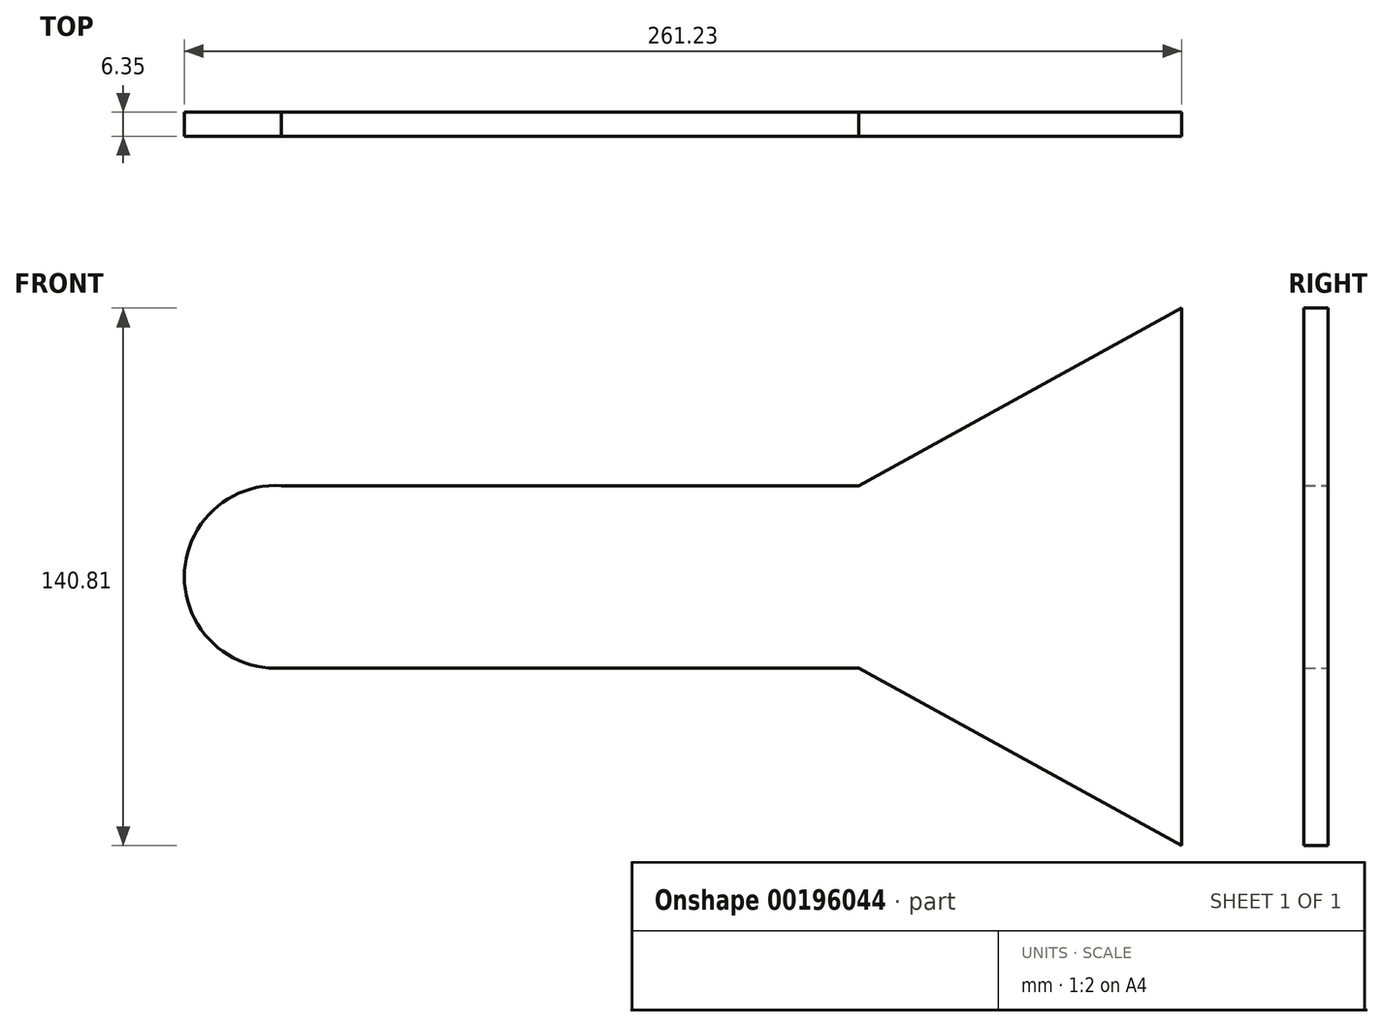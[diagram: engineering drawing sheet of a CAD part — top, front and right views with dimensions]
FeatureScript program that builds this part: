
annotation { "Feature Type Name" : "Feature", "Feature Type Description" : "" }
export const myFeature = defineFeature(function(context is Context, id is Id, definition is map)
    precondition{}
    {
        {
            var Q0;
            Q0=qCreatedBy(makeId("Front.planeOp"),FACE);
            var sketch = newSketch(context, id + "F0", { "sketchPlane" : qUnion([Q0])});
            skArc(sketch, "E0", {"start": v(-115.97, 29.82) * mm, "mid": v(-141.38, 5.93) * mm, "end": v(-115.97, -17.96) * mm});
            skLineSegment(sketch, "E1", {"start": v(-118.91, 29.82) * mm, "end": v(35.27, 29.82) * mm});
            skLineSegment(sketch, "E2", {"start": v(-118.91, -17.96) * mm, "end": v(35.27, -17.96) * mm});
            skLineSegment(sketch, "E3", {"start": v(35.27, -17.96) * mm, "end": v(119.85, -64.47) * mm});
            skLineSegment(sketch, "E4", {"start": v(119.85, -64.47) * mm, "end": v(119.85, 76.34) * mm});
            skLineSegment(sketch, "E5", {"start": v(119.85, 76.34) * mm, "end": v(35.27, 29.82) * mm});
            skSolve(sketch);
        }
        {
            var Q0;
            Q0 = qSketchRegion(id + "F0", true);
            extrude(context, id + "F1", {"entities" : qUnion([Q0]), "depth" : 6.35 * mm});
        }
    });
